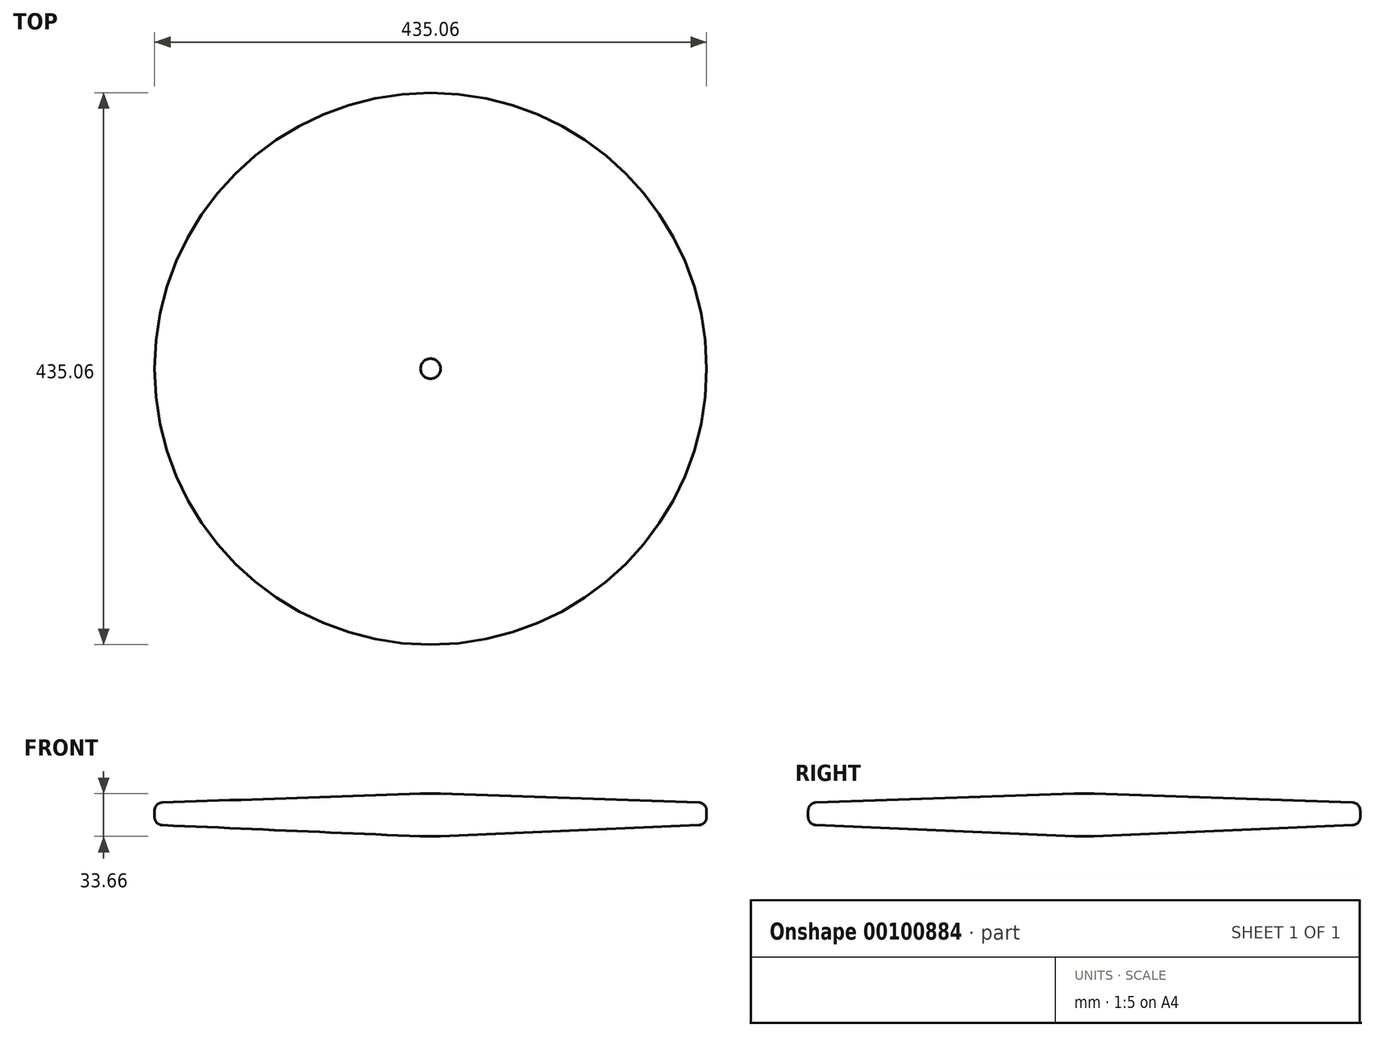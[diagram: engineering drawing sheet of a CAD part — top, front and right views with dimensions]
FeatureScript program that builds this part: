
annotation { "Feature Type Name" : "Feature", "Feature Type Description" : "" }
export const myFeature = defineFeature(function(context is Context, id is Id, definition is map)
    precondition{}
    {
        {
            var Q0;
            Q0=qCreatedBy(makeId("Front.planeOp"),FACE);
            var sketch = newSketch(context, id + "F0", { "sketchPlane" : qUnion([Q0])});
            skLineSegment(sketch, "E0", {"start": v(7.9, 15.81) * mm, "end": v(211.4, 8.88) * mm});
            skLineSegment(sketch, "E1", {"start": v(217.53, 2.53) * mm, "end": v(217.53, -2.6) * mm});
            skLineSegment(sketch, "E2", {"start": v(211.46, -8.94) * mm, "end": v(7.9, -17.85) * mm});
            skLineSegment(sketch, "E3", {"start": v(7.9, -17.85) * mm, "end": v(0, -17.85) * mm});
            skLineSegment(sketch, "E4", {"start": v(0, -17.85) * mm, "end": v(0, 15.81) * mm});
            skLineSegment(sketch, "E5", {"start": v(0, 15.81) * mm, "end": v(7.9, 15.81) * mm});
            skPoint(sketch, "E6.visualSharp", {"position": v(217.53, 8.67) * mm});
            skArc(sketch, "E6.filletArc", {"start": v(217.53, 2.53) * mm, "mid": v(215.75, 6.95) * mm, "end": v(211.4, 8.88) * mm});
            skPoint(sketch, "E7.visualSharp", {"position": v(217.53, -8.67) * mm});
            skArc(sketch, "E7.filletArc", {"start": v(211.46, -8.94) * mm, "mid": v(215.77, -6.98) * mm, "end": v(217.53, -2.6) * mm});
            skSolve(sketch);
        }
        {
            var Q0;
            Q0=makeQuery(id+"F0.imprint","IMPRINT",FACE,{"disambiguationData":[TD([[makeQuery(id+"F0.imprint","IMPRINT",EDGE,{"derivedFrom":sQuery(id+"F0.wireOp",EDGE,"E0")}),-1.0]])]});
            var Q1;
            Q1=sQuery(id+"F0.wireOp",EDGE,"E4");
            revolve(context, id + "F1", {"entities" : qUnion([Q0]), "axis" : qUnion([Q1]), "revolveType" : RevolveType.FULL});
        }
    });
